FCSTD DOCUMENT  (FreeCAD 1.0R39109 (Git))
Label: DisplayAssembly
License: All rights reserved
LicenseURL: http://en.wikipedia.org/wiki/All_rights_reserved
objects: App::Link×5, App::FeaturePython×1, Assembly::JointGroup×1, Assembly::AssemblyObject×1
EXTERNAL_REF file=DICLEDBoard.FCStd obj=LED_Ring_1
EXTERNAL_REF file=DICDispalyBoard.FCStd obj=Scale
EXTERNAL_REF file=DICMainboard.FCStd obj=Board_e9e
EXTERNAL_REF file=ConnectorInterfaceBoard.FCStd obj=Board_5996
EXTERNAL_REF file=DICAddonBoard.FCStd obj=Board_25db

FEATURE [App::Link] LED_Ring_1  label="LED_Ring 1"
  LinkPlacement = pos=(45.9471,-39.3124,2.60361) rot=(0,0,1;0rad)
  LinkedObject = -> <external DICLEDBoard.FCStd>#LED_Ring_1
  Placement = pos=(45.9471,-39.3124,2.60361) rot=(0,0,1;0rad)
FEATURE [App::Link] Scale
  LinkPlacement = pos=(46.0527,-39.5665,0.857087) rot=(-0.468143,-0.288127,-0.835359;0.008707rad)
  LinkedObject = -> <external DICDispalyBoard.FCStd>#Scale
  Placement = pos=(46.0527,-39.5665,0.857087) rot=(-0.468143,-0.288127,-0.835359;0.008707rad)
FEATURE [App::Link] DIC
  LinkedObject = -> <external DICMainboard.FCStd>#Board_e9e
FEATURE [App::FeaturePython] GroundedJoint  # Assembly grounded joint (typed FeaturePython)
  ObjectToGround = -> DIC
FEATURE [Assembly::JointGroup] Joints
  Group = -> [GroundedJoint]
FEATURE [App::Link] ConnectorInterfaceBoard
  LinkPlacement = pos=(1.90735e-06,-68.64,-15.5) rot=(1,0,0;3.14159rad)
  LinkedObject = -> <external ConnectorInterfaceBoard.FCStd>#Board_5996
  Placement = pos=(1.90735e-06,-68.64,-15.5) rot=(1,0,0;3.14159rad)
FEATURE [App::Link] DIC_Addon
  LinkPlacement = pos=(-9.53674e-07,0,-7) rot=(0,0,1;0rad)
  LinkedObject = -> <external DICAddonBoard.FCStd>#Board_25db
  Placement = pos=(-9.53674e-07,0,-7) rot=(0,0,1;0rad)
FEATURE [Assembly::AssemblyObject] Assembly
  Group = -> [Joints,LED_Ring_1,Scale,DIC,GroundedJoint,ConnectorInterfaceBoard,DIC_Addon]
  Origin = -> Origin
  Type = Assembly

RESOLVED EXTERNAL PARTS (link-assembly join: the EXTERNAL_REF files above that resolve inside this repo's crawl, each included once):
---- part ConnectorInterfaceBoard.FCStd = doc fcstd_b694cefa8e00 ----
FCSTD DOCUMENT  (FreeCAD 1.0R39109 (Git))
Label: ConnectorInterfaceBoard
License: All rights reserved
LicenseURL: http://en.wikipedia.org/wiki/All_rights_reserved
objects: Part::Feature×9, App::Part×4, App::Link×2, PartDesign::CoordinateSystem×1, Sketcher::SketchObject×1
note: 12 computed .brp shape members not serialized (recipe doc carries the construction recipe); baked Part::Feature solids carry a one-line shape summary decoded from their .brp

FEATURE [PartDesign::CoordinateSystem] Local_CS_5996
  AttacherType = Attacher::AttachEngine3D
  MapMode = 2
FEATURE [Part::Feature] Pcb_5996
  shape: bbox 56.9 x 16.76 x 1.6 mm, 40 faces (baked)
FEATURE [Sketcher::SketchObject] PCB_Sketch_5996
  ArcFitTolerance = 1e-06
  FullyConstrained = false
  MakeInternals = false
  sketch-geometry (4):
    g0: LineSegment StartX=11.938 StartY=-11.938 StartZ=0 EndX=68.834 EndY=-11.938 EndZ=0
    g1: LineSegment StartX=68.834 StartY=-11.938 StartZ=0 EndX=68.834 EndY=-28.702 EndZ=0
    g2: LineSegment StartX=68.834 StartY=-28.702 StartZ=0 EndX=11.938 EndY=-28.702 EndZ=0
    g3: LineSegment StartX=11.938 StartY=-28.702 StartZ=0 EndX=11.938 EndY=-11.938 EndZ=0
  constraints (4):
    c: Coincident(g2,g3)
    c: Coincident(g0,g3)
    c: Coincident(g1,g2)
    c: Coincident(g0,g1)
FEATURE [Part::Feature] Shape  label="J4_PinHeader_2x08_P127mm_Vertical_934e7c050846"
  Placement = pos=(16.7132,-15.875,0) rot=(0,0,1;0rad)
  shape: bbox 3.4 x 10.16 x 6.3 mm, 340 faces (baked)
FEATURE [Part::Feature] Shape001  label="J1_RT3MP_764b897103e7"
  Placement = pos=(28.829,-20.3708,16.5) rot=(0,1,0;1.5708rad)
  shape: bbox 12 x 12 x 20.5 mm, 41 faces (baked)
FEATURE [App::Link] J1_RT3MP_764b897103e7_ln_  label="J3_RT3MP_9311650603bd"
  LinkPlacement = pos=(62.865,-20.3708,16.5) rot=(0.57735,0.57735,-0.57735;2.0944rad)
  LinkedObject = -> Shape001
  Placement = pos=(62.865,-20.3708,16.5) rot=(0.57735,0.57735,-0.57735;2.0944rad)
FEATURE [App::Link] J1_RT3MP_764b897103e7_ln_001  label="J2_RT3MP_923871eb31ec"
  LinkPlacement = pos=(45.8216,-20.3962,16.5) rot=(0,1,0;1.5708rad)
  LinkedObject = -> Shape001
  Placement = pos=(45.8216,-20.3962,16.5) rot=(0,1,0;1.5708rad)
FEATURE [App::Part] Top_5996
  Group = -> [Shape,Shape001,J1_RT3MP_764b897103e7_ln_,J1_RT3MP_764b897103e7_ln_001]
  Origin = -> Origin003
FEATURE [App::Part] Step_Models_5996
  Group = -> [Top_5996]
  Origin = -> Origin002
FEATURE [Part::Feature] pads_area001  label="topPads_5996"
  Placement = pos=(0,0,0.02) rot=(0,0,1;0rad)
  shape: bbox 52.14 x 13.81 x 2e-07 mm, 53 faces, 0 solids (baked)
FEATURE [Part::Feature] Shape003  label="topTracks_5996"
  Placement = pos=(0,0,0.01) rot=(0,0,1;0rad)
  shape: bbox 46.46 x 15.71 x 2e-07 mm, 15 faces, 0 solids (baked)
FEATURE [Part::Feature] zones_area001  label="topZones_5996"
  Placement = pos=(0,0,0.01) rot=(0,0,1;0rad)
  shape: bbox 56.8 x 16.66 x 2e-07 mm, 9 faces, 0 solids (baked)
FEATURE [Part::Feature] pads_area003  label="botPads_5996"
  Placement = pos=(0,0,-1.62) rot=(0,0,1;0rad)
  shape: bbox 52.14 x 13.81 x 2e-07 mm, 53 faces, 0 solids (baked)
FEATURE [Part::Feature] Shape005  label="botTracks_5996"
  Placement = pos=(0,0,-1.61) rot=(0,0,1;0rad)
  shape: bbox 53.24 x 14.74 x 2e-07 mm, 12 faces, 0 solids (baked)
FEATURE [Part::Feature] zones_area003  label="botZones_5996"
  Placement = pos=(0,0,-1.61) rot=(0,0,1;0rad)
  shape: bbox 56.8 x 16.66 x 2e-07 mm, 1 faces, 0 solids (baked)
FEATURE [App::Part] Board_Geoms_5996
  Group = -> [Pcb_5996,PCB_Sketch_5996,pads_area001,Shape003,zones_area001,pads_area003,Shape005,zones_area003]
  Origin = -> Origin
FEATURE [App::Part] Board_5996  label="ConnectorInterfaceBoard"
  Group = -> [Local_CS_5996,Board_Geoms_5996,Step_Models_5996]
  Origin = -> Origin001
---- part DICAddonBoard.FCStd = doc fcstd_c73b9f38876c ----
FCSTD DOCUMENT  (FreeCAD 1.0R39109 (Git))
Label: DICAddonBoard
License: All rights reserved
LicenseURL: http://en.wikipedia.org/wiki/All_rights_reserved
objects: App::Link×70, Part::Feature×18, App::Part×5, PartDesign::CoordinateSystem×1, Sketcher::SketchObject×1
note: 21 computed .brp shape members not serialized (recipe doc carries the construction recipe); baked Part::Feature solids carry a one-line shape summary decoded from their .brp

FEATURE [PartDesign::CoordinateSystem] Local_CS_25db
  AttacherType = Attacher::AttachEngine3D
  MapMode = 2
FEATURE [Part::Feature] Pcb_25db
  shape: bbox 67.95 x 50.29 x 1.6 mm, 68 faces (baked)
FEATURE [Sketcher::SketchObject] PCB_Sketch_25db
  ArcFitTolerance = 1e-06
  FullyConstrained = false
  MakeInternals = false
  sketch-geometry (10):
    g0: LineSegment StartX=11.938 StartY=-11.938 StartZ=0 EndX=11.938 EndY=-62.23 EndZ=0
    g1: LineSegment StartX=68.58 StartY=-62.103 StartZ=0 EndX=79.883 EndY=-62.103 EndZ=0
    g2: LineSegment StartX=11.938 StartY=-62.23 StartZ=0 EndX=23.3806 EndY=-62.23 EndZ=0
    g3: LineSegment StartX=23.3806 StartY=-62.23 StartZ=0 EndX=23.368 EndY=-55.9897 EndZ=0
    g4: LineSegment StartX=79.756 StartY=-11.938 StartZ=0 EndX=11.938 EndY=-11.938 EndZ=0
    g5: LineSegment StartX=68.5926 StartY=-55.8627 StartZ=0 EndX=68.58 EndY=-62.103 EndZ=0
    g6: LineSegment StartX=28.448 StartY=-50.673 StartZ=0 EndX=63.5588 EndY=-50.6595 EndZ=0
    g7: LineSegment StartX=79.883 StartY=-62.103 StartZ=0 EndX=79.756 EndY=-11.938 EndZ=0
    g8: ArcOfCircle CenterX=28.5729 CenterY=-55.8776 CenterZ=0 NormalX=0 NormalY=0 NormalZ=-1 AngleXU=-0.0215457 Radius=5.20607 StartAngle=0 EndAngle=1.56835
    g9: ArcOfCircle CenterX=63.5 CenterY=-55.753 CenterZ=0 NormalX=0 NormalY=0 NormalZ=-1 AngleXU=1.58235 Radius=5.09379 StartAngle=-4.7832e-11 EndAngle=1.58079
  constraints (10):
    c: Coincident(g0,g2)
    c: Coincident(g0,g4)
    c: Coincident(g3,g8)
    c: Coincident(g2,g3)
    c: Coincident(g6,g8)
    c: Coincident(g6,g9)
    c: Coincident(g1,g5)
    c: Coincident(g5,g9)
    c: Coincident(g4,g7)
    c: Coincident(g1,g7)
FEATURE [Part::Feature] Shape  label="Q6_SOT_23_ffd5320711a5"
  Placement = pos=(37.211,-18.262,0) rot=(0,0,1;0rad)
  shape: bbox 2.5 x 3 x 1.2 mm, 76 faces (baked)
FEATURE [Part::Feature] Shape001  label="D16_D_SOD_323_d7651d96f6c3"
  Placement = pos=(13.7425,-40.366,0) rot=(0,0,1;1.5708rad)
  shape: bbox 1.25 x 2.5 x 1.1 mm, 67 faces (baked)
FEATURE [Part::Feature] Shape002  label="J6_PinSocket_2x05_P127mm_Vertical_83ee9fbb584e"
  Placement = pos=(16.891,-54.483,0) rot=(0,0,1;0rad)
  shape: bbox 3.05 x 6.35 x 7 mm, 320 faces (baked)
FEATURE [Part::Feature] Shape003  label="R41_R_0603_1608Metric_127fa2614279"
  Placement = pos=(16.433,-42.799,0) rot=(0,0,1;0rad)
  shape: bbox 1.6 x 0.8 x 0.45 mm, 26 faces (baked)
FEATURE [App::Link] R41_R_0603_1608Metric_127fa2614279_ln_  label="R12_R_0603_1608Metric_a0e0216bc4ce"
  LinkPlacement = pos=(29.9212,-15.0876,0) rot=(0,0,1;3.14159rad)
  LinkedObject = -> Shape003
  Placement = pos=(29.9212,-15.0876,0) rot=(0,0,1;3.14159rad)
FEATURE [App::Link] R41_R_0603_1608Metric_127fa2614279_ln_001  label="R13_R_0603_1608Metric_473b31106c1b"
  LinkPlacement = pos=(32.639,-18.77,0) rot=(0,0,1;1.5708rad)
  LinkedObject = -> Shape003
  Placement = pos=(32.639,-18.77,0) rot=(0,0,1;1.5708rad)
FEATURE [Part::Feature] Shape004  label="D6_D_SMA_735d77270f2b"
  Placement = pos=(55.477,-16.896,0) rot=(0,0,1;1.5708rad)
  shape: bbox 2.7 x 5 x 2.22 mm, 41 faces (baked)
FEATURE [App::Link] R41_R_0603_1608Metric_127fa2614279_ln_002  label="R9_R_0603_1608Metric_79f8a3dd54a6"
  LinkPlacement = pos=(61.214,-13.9059,0) rot=(0,0,1;3.14159rad)
  LinkedObject = -> Shape003
  Placement = pos=(61.214,-13.9059,0) rot=(0,0,1;3.14159rad)
FEATURE [App::Link] R41_R_0603_1608Metric_127fa2614279_ln_003  label="R31_R_0603_1608Metric_c49473b8d088"
  LinkPlacement = pos=(50.473,-46.8085,0) rot=(0,0,1;1.5708rad)
  LinkedObject = -> Shape003
  Placement = pos=(50.473,-46.8085,0) rot=(0,0,1;1.5708rad)
FEATURE [App::Link] R41_R_0603_1608Metric_127fa2614279_ln_004  label="R14_R_0603_1608Metric_d7197a96d642"
  LinkPlacement = pos=(37.41,-15.722,0) rot=(0,0,1;0rad)
  LinkedObject = -> Shape003
  Placement = pos=(37.41,-15.722,0) rot=(0,0,1;0rad)
FEATURE [App::Link] R41_R_0603_1608Metric_127fa2614279_ln_005  label="R35_R_0603_1608Metric_1226fcb64f1c"
  LinkPlacement = pos=(47.933,-37.9245,0) rot=(0,0,1;0rad)
  LinkedObject = -> Shape003
  Placement = pos=(47.933,-37.9245,0) rot=(0,0,1;0rad)
FEATURE [App::Link] D6_D_SMA_735d77270f2b_ln_  label="D17_D_SMA_0876cbf78d6f"
  LinkPlacement = pos=(20.828,-34.925,0) rot=(0,0,1;1.5708rad)
  LinkedObject = -> Shape004
  Placement = pos=(20.828,-34.925,0) rot=(0,0,1;1.5708rad)
FEATURE [App::Link] D6_D_SMA_735d77270f2b_ln_001  label="D15_D_SMA_1207fe425828"
  LinkPlacement = pos=(53.255,-43.21,0) rot=(0,0,1;0rad)
  LinkedObject = -> Shape004
  Placement = pos=(53.255,-43.21,0) rot=(0,0,1;0rad)
FEATURE [App::Link] D16_D_SOD_323_d7651d96f6c3_ln_  label="D13_D_SOD_323_07ad6b2cef4e"
  LinkPlacement = pos=(47.826,-32.3365,0) rot=(0,0,1;3.14159rad)
  LinkedObject = -> Shape001
  Placement = pos=(47.826,-32.3365,0) rot=(0,0,1;3.14159rad)
FEATURE [App::Link] R41_R_0603_1608Metric_127fa2614279_ln_006  label="R32_R_0603_1608Metric_48fbb2cf6ecc"
  LinkPlacement = pos=(56.061,-46.705,0) rot=(0,0,1;1.5708rad)
  LinkedObject = -> Shape003
  Placement = pos=(56.061,-46.705,0) rot=(0,0,1;1.5708rad)
FEATURE [App::Link] R41_R_0603_1608Metric_127fa2614279_ln_007  label="R24_R_0603_1608Metric_9565dda51c7b"
  LinkPlacement = pos=(50.461,-36.098,0) rot=(0,0,1;1.5708rad)
  LinkedObject = -> Shape003
  Placement = pos=(50.461,-36.098,0) rot=(0,0,1;1.5708rad)
FEATURE [App::Link] R41_R_0603_1608Metric_127fa2614279_ln_008  label="R39_R_0603_1608Metric_0d8059b3905e"
  LinkPlacement = pos=(27.857,-32.131,0) rot=(0,0,1;3.14159rad)
  LinkedObject = -> Shape003
  Placement = pos=(27.857,-32.131,0) rot=(0,0,1;3.14159rad)
FEATURE [App::Link] R41_R_0603_1608Metric_127fa2614279_ln_009  label="R11_R_0603_1608Metric_e8feb780e285"
  LinkPlacement = pos=(37.363,-14.198,0) rot=(0,0,1;0rad)
  LinkedObject = -> Shape003
  Placement = pos=(37.363,-14.198,0) rot=(0,0,1;0rad)
FEATURE [App::Link] D6_D_SMA_735d77270f2b_ln_002  label="D9_D_SMA_59bcf57c5f9f"
  LinkPlacement = pos=(51.943,-16.865,0) rot=(0,0,1;1.5708rad)
  LinkedObject = -> Shape004
  Placement = pos=(51.943,-16.865,0) rot=(0,0,1;1.5708rad)
FEATURE [App::Link] D6_D_SMA_735d77270f2b_ln_003  label="D18_D_SMA_56b2f2076145"
  LinkPlacement = pos=(24.362,-34.925,0) rot=(0,0,1;1.5708rad)
  LinkedObject = -> Shape004
  Placement = pos=(24.362,-34.925,0) rot=(0,0,1;1.5708rad)
FEATURE [App::Link] R41_R_0603_1608Metric_127fa2614279_ln_010  label="R37_R_0603_1608Metric_b9a5ae661070"
  LinkPlacement = pos=(17.25,-32.004,0) rot=(0,0,1;0rad)
  LinkedObject = -> Shape003
  Placement = pos=(17.25,-32.004,0) rot=(0,0,1;0rad)
FEATURE [App::Link] R41_R_0603_1608Metric_127fa2614279_ln_011  label="R34_R_0603_1608Metric_5b0c20e38f9c"
  LinkPlacement = pos=(44.504,-34.1145,0) rot=(0,0,1;3.14159rad)
  LinkedObject = -> Shape003
  Placement = pos=(44.504,-34.1145,0) rot=(0,0,1;3.14159rad)
FEATURE [App::Link] R41_R_0603_1608Metric_127fa2614279_ln_012  label="R33_R_0603_1608Metric_6760e7cc6251"
  LinkPlacement = pos=(44.0995,-32.3365,0) rot=(0,0,1;3.14159rad)
  LinkedObject = -> Shape003
  Placement = pos=(44.0995,-32.3365,0) rot=(0,0,1;3.14159rad)
FEATURE [App::Link] D16_D_SOD_323_d7651d96f6c3_ln_001  label="D4_D_SOD_323_fbe22daa305a"
  LinkPlacement = pos=(30.861,-18.2655,0) rot=(0,0,1;1.5708rad)
  LinkedObject = -> Shape001
  Placement = pos=(30.861,-18.2655,0) rot=(0,0,1;1.5708rad)
FEATURE [Part::Feature] Shape005  label="TH6_R_1206_3216Metric_a4174fc2a386"
  Placement = pos=(22.584,-39.624,0) rot=(0,0,1;3.14159rad)
  shape: bbox 3.2 x 1.6 x 0.55 mm, 26 faces (baked)
FEATURE [App::Link] R41_R_0603_1608Metric_127fa2614279_ln_013  label="R40_R_0603_1608Metric_99d0bb74b373"
  LinkPlacement = pos=(13.7425,-36.703,0) rot=(0,0,1;1.5708rad)
  LinkedObject = -> Shape003
  Placement = pos=(13.7425,-36.703,0) rot=(0,0,1;1.5708rad)
FEATURE [App::Link] R41_R_0603_1608Metric_127fa2614279_ln_014  label="R8_R_0603_1608Metric_f9849ceb0926"
  LinkPlacement = pos=(61.087,-19.4939,0) rot=(0,0,1;3.14159rad)
  LinkedObject = -> Shape003
  Placement = pos=(61.087,-19.4939,0) rot=(0,0,1;3.14159rad)
FEATURE [App::Link] R41_R_0603_1608Metric_127fa2614279_ln_015  label="R36_R_0603_1608Metric_b33a5e9c3cf1"
  LinkPlacement = pos=(17.377,-37.592,0) rot=(0,0,1;3.14159rad)
  LinkedObject = -> Shape003
  Placement = pos=(17.377,-37.592,0) rot=(0,0,1;3.14159rad)
FEATURE [App::Link] Q6_SOT_23_ffd5320711a5_ln_  label="Q18_SOT_23_5dae6c215293"
  LinkPlacement = pos=(16.6635,-40.259,0) rot=(0,0,1;3.14159rad)
  LinkedObject = -> Shape
  Placement = pos=(16.6635,-40.259,0) rot=(0,0,1;3.14159rad)
FEATURE [App::Link] J6_PinSocket_2x05_P127mm_Vertical_83ee9fbb584e_ln_  label="J2_PinSocket_2x05_P127mm_Vertical_fade8c78a2a7"
  LinkPlacement = pos=(76.2,-14.859,0) rot=(0,0,1;0rad)
  LinkedObject = -> Shape002
  Placement = pos=(76.2,-14.859,0) rot=(0,0,1;0rad)
FEATURE [App::Link] J6_PinSocket_2x05_P127mm_Vertical_83ee9fbb584e_ln_001  label="J5_PinSocket_2x05_P127mm_Vertical_c59673f5576a"
  LinkPlacement = pos=(16.129,-20.701,0) rot=(0,0,1;3.14159rad)
  LinkedObject = -> Shape002
  Placement = pos=(16.129,-20.701,0) rot=(0,0,1;3.14159rad)
FEATURE [App::Link] TH6_R_1206_3216Metric_a4174fc2a386_ln_  label="TH2_R_1206_3216Metric_52bc38417804"
  LinkPlacement = pos=(41.529,-18.262,0) rot=(0,0,1;1.5708rad)
  LinkedObject = -> Shape005
  Placement = pos=(41.529,-18.262,0) rot=(0,0,1;1.5708rad)
FEATURE [App::Link] D6_D_SMA_735d77270f2b_ln_004  label="D14_D_SMA_40db2f55f09c"
  LinkPlacement = pos=(53.255,-39.584,0) rot=(0,0,1;0rad)
  LinkedObject = -> Shape004
  Placement = pos=(53.255,-39.584,0) rot=(0,0,1;0rad)
FEATURE [App::Link] R41_R_0603_1608Metric_127fa2614279_ln_016  label="R42_R_0603_1608Metric_3962cb7ffa21"
  LinkPlacement = pos=(19.3305,-40.386,0) rot=(0,0,1;1.5708rad)
  LinkedObject = -> Shape003
  Placement = pos=(19.3305,-40.386,0) rot=(0,0,1;1.5708rad)
FEATURE [App::Link] J6_PinSocket_2x05_P127mm_Vertical_83ee9fbb584e_ln_002  label="J4_PinSocket_2x05_P127mm_Vertical_839abc38b667"
  LinkPlacement = pos=(75.819,-54.473,0) rot=(0,0,1;0rad)
  LinkedObject = -> Shape002
  Placement = pos=(75.819,-54.473,0) rot=(0,0,1;0rad)
FEATURE [App::Link] R41_R_0603_1608Metric_127fa2614279_ln_017  label="R10_R_0603_1608Metric_f7e09fcf0586"
  LinkPlacement = pos=(48.387,-13.563,0) rot=(0,0,1;3.14159rad)
  LinkedObject = -> Shape003
  Placement = pos=(48.387,-13.563,0) rot=(0,0,1;3.14159rad)
FEATURE [App::Link] R41_R_0603_1608Metric_127fa2614279_ln_018  label="R38_R_0603_1608Metric_5053fa264887"
  LinkPlacement = pos=(27.984,-37.719,0) rot=(0,0,1;3.14159rad)
  LinkedObject = -> Shape003
  Placement = pos=(27.984,-37.719,0) rot=(0,0,1;3.14159rad)
FEATURE [App::Link] R41_R_0603_1608Metric_127fa2614279_ln_019  label="R30_R_0603_1608Metric_0ef8a02bf31b"
  LinkPlacement = pos=(56.061,-36.0085,0) rot=(0,0,-1;1.5708rad)
  LinkedObject = -> Shape003
  Placement = pos=(56.061,-36.0085,0) rot=(0,0,-1;1.5708rad)
FEATURE [App::Link] Q6_SOT_23_ffd5320711a5_ln_001  label="Q15_SOT_23_f88ca606a138"
  LinkPlacement = pos=(47.933,-35.2575,0) rot=(0,0,1;1.5708rad)
  LinkedObject = -> Shape
  Placement = pos=(47.933,-35.2575,0) rot=(0,0,1;1.5708rad)
FEATURE [App::Link] TH6_R_1206_3216Metric_a4174fc2a386_ln_001  label="TH4_R_1206_3216Metric_6cedd577e318"
  LinkPlacement = pos=(48.568,-41.178,0) rot=(0,0,1;1.5708rad)
  LinkedObject = -> Shape005
  Placement = pos=(48.568,-41.178,0) rot=(0,0,1;1.5708rad)
FEATURE [App::Part] Top_25db
  Group = -> [Shape,Shape001,Shape002,Shape003,R41_R_0603_1608Metric_127fa2614279_ln_,R41_R_0603_1608Metric_127fa2614279_ln_001,Shape004,R41_R_0603_1608Metric_127fa2614279_ln_002,R41_R_0603_1608Metric_127fa2614279_ln_003,R41_R_0603_1608Metric_127fa2614279_ln_004,R41_R_0603_1608Metric_127fa2614279_ln_005,D6_D_SMA_735d77270f2b_ln_,D6_D_SMA_735d77270f2b_ln_001,D16_D_SOD_323_d7651d96f6c3_ln_,+26 more]
  Origin = -> Origin003
FEATURE [App::Link] R41_R_0603_1608Metric_127fa2614279_ln_020  label="R16_R_0603_1608Metric_7932c1e08af1"
  LinkPlacement = pos=(41.275,-42.313,-1.6) rot=(0.707107,0.707107,0;3.14159rad)
  LinkedObject = -> Shape003
  Placement = pos=(41.275,-42.313,-1.6) rot=(0.707107,0.707107,0;3.14159rad)
FEATURE [App::Link] R41_R_0603_1608Metric_127fa2614279_ln_021  label="R25_R_0603_1608Metric_af43064dc6b6"
  LinkPlacement = pos=(74.996,-34.8215,-1.6) rot=(0.707107,-0.707107,0;3.14159rad)
  LinkedObject = -> Shape003
  Placement = pos=(74.996,-34.8215,-1.6) rot=(0.707107,-0.707107,0;3.14159rad)
FEATURE [App::Link] R41_R_0603_1608Metric_127fa2614279_ln_022  label="R3_R_0603_1608Metric_90eb9fac611c"
  LinkPlacement = pos=(27.8525,-37.777,-1.6) rot=(0.707107,0.707107,0;3.14159rad)
  LinkedObject = -> Shape003
  Placement = pos=(27.8525,-37.777,-1.6) rot=(0.707107,0.707107,0;3.14159rad)
FEATURE [App::Link] R41_R_0603_1608Metric_127fa2614279_ln_023  label="R2_R_0603_1608Metric_a95339afed33"
  LinkPlacement = pos=(22.3534,-27.095,-1.6) rot=(0.707107,0.707107,0;3.14159rad)
  LinkedObject = -> Shape003
  Placement = pos=(22.3534,-27.095,-1.6) rot=(0.707107,0.707107,0;3.14159rad)
FEATURE [App::Link] R41_R_0603_1608Metric_127fa2614279_ln_024  label="R29_R_0603_1608Metric_a323e5d2541c"
  LinkPlacement = pos=(69.088,-31.2255,-1.6) rot=(0.707107,-0.707107,0;3.14159rad)
  LinkedObject = -> Shape003
  Placement = pos=(69.088,-31.2255,-1.6) rot=(0.707107,-0.707107,0;3.14159rad)
FEATURE [App::Link] R41_R_0603_1608Metric_127fa2614279_ln_025  label="R1_R_0603_1608Metric_b07fb1c3085f"
  LinkPlacement = pos=(27.9414,-27.222,-1.6) rot=(0.707107,0.707107,0;3.14159rad)
  LinkedObject = -> Shape003
  Placement = pos=(27.9414,-27.222,-1.6) rot=(0.707107,0.707107,0;3.14159rad)
FEATURE [App::Link] R41_R_0603_1608Metric_127fa2614279_ln_026  label="R18_R_0603_1608Metric_5d82281689e8"
  LinkPlacement = pos=(26.7885,-42.672,-1.6) rot=(0,1,0;3.14159rad)
  LinkedObject = -> Shape003
  Placement = pos=(26.7885,-42.672,-1.6) rot=(0,1,0;3.14159rad)
FEATURE [App::Link] R41_R_0603_1608Metric_127fa2614279_ln_027  label="R27_R_0603_1608Metric_214af474eae8"
  LinkPlacement = pos=(75.9085,-41.275,-1.6) rot=(1,0,0;3.14159rad)
  LinkedObject = -> Shape003
  Placement = pos=(75.9085,-41.275,-1.6) rot=(1,0,0;3.14159rad)
FEATURE [App::Link] D6_D_SMA_735d77270f2b_ln_005  label="D11_D_SMA_1ba17688d2f4"
  LinkPlacement = pos=(38.449,-38.735,-1.6) rot=(1,0,0;3.14159rad)
  LinkedObject = -> Shape004
  Placement = pos=(38.449,-38.735,-1.6) rot=(1,0,0;3.14159rad)
FEATURE [App::Link] R41_R_0603_1608Metric_127fa2614279_ln_028  label="R17_R_0603_1608Metric_89ce4ec7833c"
  LinkPlacement = pos=(26.8355,-48.26,-1.6) rot=(1,0,0;3.14159rad)
  LinkedObject = -> Shape003
  Placement = pos=(26.8355,-48.26,-1.6) rot=(1,0,0;3.14159rad)
FEATURE [App::Link] R41_R_0603_1608Metric_127fa2614279_ln_029  label="R6_R_0603_1608Metric_1afd86b5277d"
  LinkPlacement = pos=(35.7265,-28.421,-1.6) rot=(0.707107,0.707107,0;3.14159rad)
  LinkedObject = -> Shape003
  Placement = pos=(35.7265,-28.421,-1.6) rot=(0.707107,0.707107,0;3.14159rad)
FEATURE [App::Link] D16_D_SOD_323_d7651d96f6c3_ln_002  label="D10_D_SOD_323_00e277693b72"
  LinkPlacement = pos=(33.167,-46.0745,-1.6) rot=(0,1,0;3.14159rad)
  LinkedObject = -> Shape001
  Placement = pos=(33.167,-46.0745,-1.6) rot=(0,1,0;3.14159rad)
FEATURE [Part::Feature] Shape006  label="J3_PinHeader_2x08_P127mm_Vertical_13ff719d442c"
  Placement = pos=(50.551,-23.866,-1.6) rot=(0.707107,0.707107,0;3.14159rad)
  shape: bbox 10.16 x 3.4 x 6.3 mm, 340 faces (baked)
FEATURE [App::Link] D6_D_SMA_735d77270f2b_ln_006  label="D3_D_SMA_cd35c1e422c8"
  LinkPlacement = pos=(25.0905,-34.268,-1.6) rot=(0,1,0;3.14159rad)
  LinkedObject = -> Shape004
  Placement = pos=(25.0905,-34.268,-1.6) rot=(0,1,0;3.14159rad)
FEATURE [App::Link] R41_R_0603_1608Metric_127fa2614279_ln_030  label="R7_R_0603_1608Metric_afc0888e760f"
  LinkPlacement = pos=(30.6465,-28.172,-1.6) rot=(0.707107,-0.707107,0;3.14159rad)
  LinkedObject = -> Shape003
  Placement = pos=(30.6465,-28.172,-1.6) rot=(0.707107,-0.707107,0;3.14159rad)
FEATURE [App::Link] R41_R_0603_1608Metric_127fa2614279_ln_031  label="R28_R_0603_1608Metric_a4707fec901c"
  LinkPlacement = pos=(61.595,-31.0515,-1.6) rot=(0.707107,0.707107,0;3.14159rad)
  LinkedObject = -> Shape003
  Placement = pos=(61.595,-31.0515,-1.6) rot=(0.707107,0.707107,0;3.14159rad)
FEATURE [App::Link] D16_D_SOD_323_d7651d96f6c3_ln_003  label="D5_D_SOD_323_8140ef0d37c0"
  LinkPlacement = pos=(63.373,-31.095,-1.6) rot=(0.707107,0.707107,0;3.14159rad)
  LinkedObject = -> Shape001
  Placement = pos=(63.373,-31.095,-1.6) rot=(0.707107,0.707107,0;3.14159rad)
FEATURE [App::Link] D16_D_SOD_323_d7651d96f6c3_ln_004  label="D1_D_SOD_323_d5d77308ac17"
  LinkPlacement = pos=(33.1665,-31.347,-1.6) rot=(1,0,0;3.14159rad)
  LinkedObject = -> Shape001
  Placement = pos=(33.1665,-31.347,-1.6) rot=(1,0,0;3.14159rad)
FEATURE [App::Link] Q6_SOT_23_ffd5320711a5_ln_002  label="Q10_SOT_23_8cad5c28a702"
  LinkPlacement = pos=(33.147,-43.0265,-1.6) rot=(0.707107,-0.707107,0;3.14159rad)
  LinkedObject = -> Shape
  Placement = pos=(33.147,-43.0265,-1.6) rot=(0.707107,-0.707107,0;3.14159rad)
FEATURE [App::Link] R41_R_0603_1608Metric_127fa2614279_ln_032  label="R23_R_0603_1608Metric_7848ec0b3468"
  LinkPlacement = pos=(65.151,-41.529,-1.6) rot=(1,0,0;3.14159rad)
  LinkedObject = -> Shape003
  Placement = pos=(65.151,-41.529,-1.6) rot=(1,0,0;3.14159rad)
FEATURE [App::Link] TH6_R_1206_3216Metric_a4174fc2a386_ln_002  label="TH5_R_1206_3216Metric_65273da20f15"
  LinkPlacement = pos=(70.612,-34.036,-1.6) rot=(0,1,0;3.14159rad)
  LinkedObject = -> Shape005
  Placement = pos=(70.612,-34.036,-1.6) rot=(0,1,0;3.14159rad)
FEATURE [App::Link] R41_R_0603_1608Metric_127fa2614279_ln_033  label="R19_R_0603_1608Metric_b451ed5a0d5d"
  LinkPlacement = pos=(29.845,-41.021,-1.6) rot=(0.707107,-0.707107,0;3.14159rad)
  LinkedObject = -> Shape003
  Placement = pos=(29.845,-41.021,-1.6) rot=(0.707107,-0.707107,0;3.14159rad)
FEATURE [App::Link] R41_R_0603_1608Metric_127fa2614279_ln_034  label="R21_R_0603_1608Metric_086685fbb64e"
  LinkPlacement = pos=(64.262,-35.0285,-1.6) rot=(0.707107,0.707107,0;3.14159rad)
  LinkedObject = -> Shape003
  Placement = pos=(64.262,-35.0285,-1.6) rot=(0.707107,0.707107,0;3.14159rad)
FEATURE [App::Link] R41_R_0603_1608Metric_127fa2614279_ln_035  label="R20_R_0603_1608Metric_74876393d18b"
  LinkPlacement = pos=(37.211,-46.0745,-1.6) rot=(1,0,0;3.14159rad)
  LinkedObject = -> Shape003
  Placement = pos=(37.211,-46.0745,-1.6) rot=(1,0,0;3.14159rad)
FEATURE [App::Link] R41_R_0603_1608Metric_127fa2614279_ln_036  label="R15_R_0603_1608Metric_62f7b17bc8fc"
  LinkPlacement = pos=(35.687,-42.313,-1.6) rot=(0.707107,-0.707107,0;3.14159rad)
  LinkedObject = -> Shape003
  Placement = pos=(35.687,-42.313,-1.6) rot=(0.707107,-0.707107,0;3.14159rad)
FEATURE [App::Link] D6_D_SMA_735d77270f2b_ln_007  label="D2_D_SMA_e8f0f4ea1691"
  LinkPlacement = pos=(25.0905,-30.734,-1.6) rot=(0,1,0;3.14159rad)
  LinkedObject = -> Shape004
  Placement = pos=(25.0905,-30.734,-1.6) rot=(0,1,0;3.14159rad)
FEATURE [App::Link] TH6_R_1206_3216Metric_a4174fc2a386_ln_003  label="TH1_R_1206_3216Metric_ce9414de59a2"
  LinkPlacement = pos=(29.8845,-32.617,-1.6) rot=(0.707107,0.707107,0;3.14159rad)
  LinkedObject = -> Shape005
  Placement = pos=(29.8845,-32.617,-1.6) rot=(0.707107,0.707107,0;3.14159rad)
FEATURE [App::Link] D6_D_SMA_735d77270f2b_ln_008  label="D12_D_SMA_21d0ff51f2b2"
  LinkPlacement = pos=(38.449,-35.201,-1.6) rot=(1,0,0;3.14159rad)
  LinkedObject = -> Shape004
  Placement = pos=(38.449,-35.201,-1.6) rot=(1,0,0;3.14159rad)
FEATURE [App::Link] TH6_R_1206_3216Metric_a4174fc2a386_ln_004  label="TH3_R_1206_3216Metric_be97d367e00d"
  LinkPlacement = pos=(33.782,-36.852,-1.6) rot=(0.707107,-0.707107,0;3.14159rad)
  LinkedObject = -> Shape005
  Placement = pos=(33.782,-36.852,-1.6) rot=(0.707107,-0.707107,0;3.14159rad)
FEATURE [App::Link] D6_D_SMA_735d77270f2b_ln_009  label="D8_D_SMA_7218f854b2e2"
  LinkPlacement = pos=(72.39,-38.703,-1.6) rot=(0.707107,-0.707107,0;3.14159rad)
  LinkedObject = -> Shape004
  Placement = pos=(72.39,-38.703,-1.6) rot=(0.707107,-0.707107,0;3.14159rad)
FEATURE [App::Link] Q6_SOT_23_ffd5320711a5_ln_003  label="Q3_SOT_23_dc7f19c19d1b"
  LinkPlacement = pos=(33.1865,-28.299,-1.6) rot=(0.707107,-0.707107,0;3.14159rad)
  LinkedObject = -> Shape
  Placement = pos=(33.1865,-28.299,-1.6) rot=(0.707107,-0.707107,0;3.14159rad)
FEATURE [App::Link] R41_R_0603_1608Metric_127fa2614279_ln_037  label="R4_R_0603_1608Metric_2e89caf32d98"
  LinkPlacement = pos=(22.2645,-37.8005,-1.6) rot=(0.707107,-0.707107,0;3.14159rad)
  LinkedObject = -> Shape003
  Placement = pos=(22.2645,-37.8005,-1.6) rot=(0.707107,-0.707107,0;3.14159rad)
FEATURE [App::Link] R41_R_0603_1608Metric_127fa2614279_ln_038  label="R22_R_0603_1608Metric_94414fea2e43"
  LinkPlacement = pos=(33.1235,-40.3595,-1.6) rot=(1,0,0;3.14159rad)
  LinkedObject = -> Shape003
  Placement = pos=(33.1235,-40.3595,-1.6) rot=(1,0,0;3.14159rad)
FEATURE [App::Link] D6_D_SMA_735d77270f2b_ln_010  label="D7_D_SMA_2e44e889cb4e"
  LinkPlacement = pos=(68.834,-38.703,-1.6) rot=(0.707107,-0.707107,0;3.14159rad)
  LinkedObject = -> Shape004
  Placement = pos=(68.834,-38.703,-1.6) rot=(0.707107,-0.707107,0;3.14159rad)
FEATURE [App::Link] R41_R_0603_1608Metric_127fa2614279_ln_039  label="R26_R_0603_1608Metric_d41138b5fa4f"
  LinkPlacement = pos=(64.389,-28.281,-1.6) rot=(1,0,0;3.14159rad)
  LinkedObject = -> Shape003
  Placement = pos=(64.389,-28.281,-1.6) rot=(1,0,0;3.14159rad)
FEATURE [App::Link] Q6_SOT_23_ffd5320711a5_ln_004  label="Q12_SOT_23_6e3906f2bc9c"
  LinkPlacement = pos=(66.421,-31.202,-1.6) rot=(0,1,0;3.14159rad)
  LinkedObject = -> Shape
  Placement = pos=(66.421,-31.202,-1.6) rot=(0,1,0;3.14159rad)
FEATURE [App::Link] R41_R_0603_1608Metric_127fa2614279_ln_040  label="R5_R_0603_1608Metric_a69d22cc4bcb"
  LinkPlacement = pos=(37.719,-30.353,-1.6) rot=(0.707107,0.707107,0;3.14159rad)
  LinkedObject = -> Shape003
  Placement = pos=(37.719,-30.353,-1.6) rot=(0.707107,0.707107,0;3.14159rad)
FEATURE [App::Part] Bot_25db
  Group = -> [R41_R_0603_1608Metric_127fa2614279_ln_020,R41_R_0603_1608Metric_127fa2614279_ln_021,R41_R_0603_1608Metric_127fa2614279_ln_022,R41_R_0603_1608Metric_127fa2614279_ln_023,R41_R_0603_1608Metric_127fa2614279_ln_024,R41_R_0603_1608Metric_127fa2614279_ln_025,R41_R_0603_1608Metric_127fa2614279_ln_026,R41_R_0603_1608Metric_127fa2614279_ln_027,D6_D_SMA_735d77270f2b_ln_005,+28 more]
  Origin = -> Origin004
FEATURE [App::Part] Step_Models_25db
  Group = -> [Top_25db,Bot_25db]
  Origin = -> Origin002
FEATURE [Part::Feature] pads_area001  label="topPads_25db"
  Placement = pos=(0,0,0.02) rot=(0,0,1;0rad)
  shape: bbox 65.44 x 47.07 x 2e-07 mm, 247 faces, 0 solids (baked)
FEATURE [Part::Feature] Shape008  label="topTracks_25db"
  Placement = pos=(0,0,0.01) rot=(0,0,1;0rad)
  shape: bbox 65.02 x 45.59 x 2e-07 mm, 81 faces, 0 solids (baked)
FEATURE [Part::Feature] pads_area003  label="botPads_25db"
  Placement = pos=(0,0,-1.62) rot=(0,0,1;0rad)
  shape: bbox 65.44 x 47.03 x 2e-07 mm, 248 faces, 0 solids (baked)
FEATURE [Part::Feature] Shape010  label="botTracks_25db"
  Placement = pos=(0,0,-1.61) rot=(0,0,1;0rad)
  shape: bbox 65.32 x 46.99 x 2e-07 mm, 80 faces, 0 solids (baked)
FEATURE [Part::Feature] botSilks_c76e
  Placement = pos=(0,0,-1.67) rot=(0,0,1;0rad)
  shape: bbox 83.53 x 49.14 x 2e-07 mm, 230 faces, 0 solids (baked)
FEATURE [Part::Feature] topSilks_caba
  Placement = pos=(0,0,0.07) rot=(0,0,1;0rad)
  shape: bbox 64.67 x 49.71 x 2e-07 mm, 286 faces, 0 solids (baked)
FEATURE [Part::Feature] Part__Feature  label="1"
  Placement = pos=(16.4,-27.2,-1.6) rot=(0,1,0;3.14159rad)
  shape: bbox 6 x 6 x 5.6 mm, 7 faces (baked)
FEATURE [Part::Feature] Part__Feature001  label="1001"
  Placement = pos=(67.9,-16.9,-1.6) rot=(0,1,0;3.14159rad)
  shape: bbox 6 x 6 x 5.6 mm, 7 faces (baked)
FEATURE [Part::Feature] Part__Feature002  label="1002"
  Placement = pos=(16.4,-48,-1.6) rot=(0,1,0;3.14159rad)
  shape: bbox 6 x 6 x 5.6 mm, 7 faces (baked)
FEATURE [Part::Feature] Part__Feature003  label="1003"
  Placement = pos=(74.4,-47.8,-1.6) rot=(0,1,0;3.14159rad)
  shape: bbox 6 x 6 x 5.6 mm, 7 faces (baked)
FEATURE [App::Part] Board_Geoms_25db
  Group = -> [Pcb_25db,PCB_Sketch_25db,pads_area001,Shape008,pads_area003,Shape010,botSilks_c76e,topSilks_caba,Part__Feature,Part__Feature001,Part__Feature002,Part__Feature003]
  Origin = -> Origin
FEATURE [App::Part] Board_25db  label="DIC_Addon"
  Group = -> [Local_CS_25db,Board_Geoms_25db,Step_Models_25db]
  Origin = -> Origin001
---- part DICDispalyBoard.FCStd = doc fcstd_930c7f865829 ----
FCSTD DOCUMENT  (FreeCAD 1.0R39109 (Git))
Label: DICDispalyBoard
License: All rights reserved
LicenseURL: http://en.wikipedia.org/wiki/All_rights_reserved
objects: Part::Feature×1, Part::Scale×1
note: 2 computed .brp shape members not serialized (recipe doc carries the construction recipe); baked Part::Feature solids carry a one-line shape summary decoded from their .brp

FEATURE [Part::Feature] Part__Feature  label="78901133-5F87-439E-955A-E59BF70E4BD8"
  shape: bbox 55 x 43.5 x 6.701 mm, 1221 faces, 4 solids (baked)
FEATURE [Part::Scale] Scale
  Base = -> Part__Feature
  Uniform = false
  UniformScale = 1
  XScale = 1
  YScale = 1.12
  ZScale = 1
---- part DICMainboard.FCStd = doc fcstd_b85fe997ea7c ----
FCSTD DOCUMENT  (FreeCAD 1.0R39109 (Git))
Label: DICMainboard
License: All rights reserved
LicenseURL: http://en.wikipedia.org/wiki/All_rights_reserved
objects: App::Link×97, Part::Feature×24, App::Part×10, PartDesign::CoordinateSystem×1, Sketcher::SketchObject×1
note: 27 computed .brp shape members not serialized (recipe doc carries the construction recipe); baked Part::Feature solids carry a one-line shape summary decoded from their .brp

FEATURE [PartDesign::CoordinateSystem] Local_CS_e9e
  AttacherType = Attacher::AttachEngine3D
  MapMode = 2
FEATURE [Part::Feature] Pcb_e9e
  shape: bbox 68.07 x 55.25 x 1.6 mm, 110 faces (baked)
FEATURE [Sketcher::SketchObject] PCB_Sketch_e9e
  ArcFitTolerance = 1e-06
  FullyConstrained = true
  MakeInternals = false
FEATURE [Part::Feature] Shape  label="C19_C_0805_2012Metric_915db11c73f1"
  Placement = pos=(24.257,-16.448,-1.6) rot=(0.707107,0.707107,0;3.14159rad)
  shape: bbox 1.25 x 2 x 1.25 mm, 28 faces (baked)
FEATURE [Part::Feature] Shape001  label="C18_C_0603_1608Metric_10e447ca614a"
  Placement = pos=(39.878,-20.193,-1.6) rot=(1,0,0;3.14159rad)
  shape: bbox 1.6 x 0.8 x 0.8 mm, 28 faces (baked)
FEATURE [Part::Feature] Shape002  label="R42_R_0603_1608Metric_e00ced120b5b"
  Placement = pos=(70.993,-25.146,-1.6) rot=(1,0,0;3.14159rad)
  shape: bbox 1.6 x 0.8 x 0.45 mm, 26 faces (baked)
FEATURE [App::Link] R42_R_0603_1608Metric_e00ced120b5b_ln_  label="R3_R_0603_1608Metric_9b0ed8f2439a"
  LinkPlacement = pos=(35.687,-42.037,-1.6) rot=(1,0,0;3.14159rad)
  LinkedObject = -> Shape002
  Placement = pos=(35.687,-42.037,-1.6) rot=(1,0,0;3.14159rad)
FEATURE [App::Link] R42_R_0603_1608Metric_e00ced120b5b_ln_001  label="R2_R_0603_1608Metric_8df39385d074"
  LinkPlacement = pos=(27.265,-19.939,-1.6) rot=(0,1,0;3.14159rad)
  LinkedObject = -> Shape002
  Placement = pos=(27.265,-19.939,-1.6) rot=(0,1,0;3.14159rad)
FEATURE [Part::Feature] Shape003  label="C21_CP_Radial_D80mm_P350mm_b4bb79b80bd8"
  Placement = pos=(28.067,-57.531,-1.6) rot=(0.707107,0.707107,0;3.14159rad)
  shape: bbox 10.23 x 9.886 x 10 mm, 54 faces (baked)
FEATURE [App::Link] C19_C_0805_2012Metric_915db11c73f1_ln_  label="C12_C_0805_2012Metric_6993a4fefcef"
  LinkPlacement = pos=(29.972,-40.386,-1.6) rot=(0,1,0;3.14159rad)
  LinkedObject = -> Shape
  Placement = pos=(29.972,-40.386,-1.6) rot=(0,1,0;3.14159rad)
FEATURE [Part::Feature] Shape004  label="JTAG1_PinHeader_2x07_P127mm_Vertical_7ea92a9874db"
  Placement = pos=(76.835,-29.718,-1.6) rot=(0,1,0;3.14159rad)
  shape: bbox 3.4 x 8.89 x 6.3 mm, 298 faces (baked)
FEATURE [App::Link] R42_R_0603_1608Metric_e00ced120b5b_ln_002  label="R29_R_0603_1608Metric_b834401a76b2"
  LinkPlacement = pos=(60.579,-46.228,-1.6) rot=(0,1,0;3.14159rad)
  LinkedObject = -> Shape002
  Placement = pos=(60.579,-46.228,-1.6) rot=(0,1,0;3.14159rad)
FEATURE [App::Link] C18_C_0603_1608Metric_10e447ca614a_ln_  label="C29_C_0603_1608Metric_30aa2c5fb68f"
  LinkPlacement = pos=(50.546,-26.035,-1.6) rot=(1,0,0;3.14159rad)
  LinkedObject = -> Shape001
  Placement = pos=(50.546,-26.035,-1.6) rot=(1,0,0;3.14159rad)
FEATURE [App::Link] R42_R_0603_1608Metric_e00ced120b5b_ln_003  label="R36_R_0603_1608Metric_5693be527eb2"
  LinkPlacement = pos=(53.848,-26.035,-1.6) rot=(0,1,0;3.14159rad)
  LinkedObject = -> Shape002
  Placement = pos=(53.848,-26.035,-1.6) rot=(0,1,0;3.14159rad)
FEATURE [App::Link] R42_R_0603_1608Metric_e00ced120b5b_ln_004  label="R39_R_0603_1608Metric_50952633201f"
  LinkPlacement = pos=(69.215,-29.845,-1.6) rot=(0.707107,0.707107,0;3.14159rad)
  LinkedObject = -> Shape002
  Placement = pos=(69.215,-29.845,-1.6) rot=(0.707107,0.707107,0;3.14159rad)
FEATURE [Part::Feature] Shape005  label="U2_SOT_23_5143090a7d01"
  Placement = pos=(31.877,-43.688,-1.6) rot=(0.707107,-0.707107,0;3.14159rad)
  shape: bbox 3 x 2.5 x 1.2 mm, 76 faces (baked)
FEATURE [App::Link] U2_SOT_23_5143090a7d01_ln_  label="Q2_SOT_23_a46526c7cbaa"
  LinkPlacement = pos=(65.786,-38.735,-1.6) rot=(0.707107,0.707107,0;3.14159rad)
  LinkedObject = -> Shape005
  Placement = pos=(65.786,-38.735,-1.6) rot=(0.707107,0.707107,0;3.14159rad)
FEATURE [App::Link] R42_R_0603_1608Metric_e00ced120b5b_ln_005  label="R31_R_0603_1608Metric_b000aee3d83a"
  LinkPlacement = pos=(59.309,-28.702,-1.6) rot=(0,1,0;3.14159rad)
  LinkedObject = -> Shape002
  Placement = pos=(59.309,-28.702,-1.6) rot=(0,1,0;3.14159rad)
FEATURE [App::Link] C18_C_0603_1608Metric_10e447ca614a_ln_001  label="C5_C_0603_1608Metric_679d8c6e1927"
  LinkPlacement = pos=(34.417,-44.45,-1.6) rot=(0.707107,0.707107,0;3.14159rad)
  LinkedObject = -> Shape001
  Placement = pos=(34.417,-44.45,-1.6) rot=(0.707107,0.707107,0;3.14159rad)
FEATURE [App::Link] C18_C_0603_1608Metric_10e447ca614a_ln_002  label="C6_C_0603_1608Metric_e41e872100cf"
  LinkPlacement = pos=(39.116,-24.322,-1.6) rot=(0,1,0;3.14159rad)
  LinkedObject = -> Shape001
  Placement = pos=(39.116,-24.322,-1.6) rot=(0,1,0;3.14159rad)
FEATURE [Part::Feature] Shape006  label="12VGood1_LED_0805_2012Metric_2ad75f4ca093"
  Placement = pos=(69.469,-36.195,-1.6) rot=(0,1,0;3.14159rad)
  shape: bbox 2 x 1.25 x 1.1 mm, 50 faces (baked)
FEATURE [App::Link] C19_C_0805_2012Metric_915db11c73f1_ln_001  label="C14_C_0805_2012Metric_060f63ed2ef4"
  LinkPlacement = pos=(42.418,-49.911,-1.6) rot=(1,0,0;3.14159rad)
  LinkedObject = -> Shape
  Placement = pos=(42.418,-49.911,-1.6) rot=(1,0,0;3.14159rad)
FEATURE [App::Link] R42_R_0603_1608Metric_e00ced120b5b_ln_006  label="R30_R_0603_1608Metric_8c3fd63a3134"
  LinkPlacement = pos=(50.8,-42.926,-1.6) rot=(0,1,0;3.14159rad)
  LinkedObject = -> Shape002
  Placement = pos=(50.8,-42.926,-1.6) rot=(0,1,0;3.14159rad)
FEATURE [App::Link] C18_C_0603_1608Metric_10e447ca614a_ln_003  label="C17_C_0603_1608Metric_5bd1929c3623"
  LinkPlacement = pos=(39.878,-21.971,-1.6) rot=(1,0,0;3.14159rad)
  LinkedObject = -> Shape001
  Placement = pos=(39.878,-21.971,-1.6) rot=(1,0,0;3.14159rad)
FEATURE [App::Link] R42_R_0603_1608Metric_e00ced120b5b_ln_007  label="R25_R_0603_1608Metric_14260ea3fd4e"
  LinkPlacement = pos=(64.77,-44.704,-1.6) rot=(0,1,0;3.14159rad)
  LinkedObject = -> Shape002
  Placement = pos=(64.77,-44.704,-1.6) rot=(0,1,0;3.14159rad)
FEATURE [Part::Feature] Shape007  label="U10_MSOP_8_3x3mm_P065mm_82bb67e16242"
  Placement = pos=(63.5,-23.241,-1.6) rot=(0.707107,0.707107,0;3.14159rad)
  shape: bbox 3 x 4.9 x 0.95 mm, 156 faces (baked)
FEATURE [App::Link] U2_SOT_23_5143090a7d01_ln_001  label="Q1_SOT_23_1223d9ad7d7e"
  LinkPlacement = pos=(68.072,-33.274,-1.6) rot=(1,0,0;3.14159rad)
  LinkedObject = -> Shape005
  Placement = pos=(68.072,-33.274,-1.6) rot=(1,0,0;3.14159rad)
FEATURE [App::Link] C19_C_0805_2012Metric_915db11c73f1_ln_002  label="C11_C_0805_2012Metric_20aa78c893d6"
  LinkPlacement = pos=(54.2075,-49.53,-1.6) rot=(0,1,0;3.14159rad)
  LinkedObject = -> Shape
  Placement = pos=(54.2075,-49.53,-1.6) rot=(0,1,0;3.14159rad)
FEATURE [Part::Feature] Shape008  label="J3_PinHeader_2x05_P127mm_Vertical_4a0e541a8516"
  Placement = pos=(75.819,-54.473,-1.6) rot=(0,1,0;3.14159rad)
  shape: bbox 3.4 x 6.35 x 6.3 mm, 214 faces (baked)
FEATURE [App::Link] R42_R_0603_1608Metric_e00ced120b5b_ln_008  label="R1_R_0603_1608Metric_52185c8e4965"
  LinkPlacement = pos=(27.265,-22.733,-1.6) rot=(1,0,0;3.14159rad)
  LinkedObject = -> Shape002
  Placement = pos=(27.265,-22.733,-1.6) rot=(1,0,0;3.14159rad)
FEATURE [App::Link] C19_C_0805_2012Metric_915db11c73f1_ln_003  label="C7_C_0805_2012Metric_b3b50e9b0364"
  LinkPlacement = pos=(50.2705,-49.53,-1.6) rot=(1,0,0;3.14159rad)
  LinkedObject = -> Shape
  Placement = pos=(50.2705,-49.53,-1.6) rot=(1,0,0;3.14159rad)
FEATURE [App::Link] U10_MSOP_8_3x3mm_P065mm_82bb67e16242_ln_  label="U9_MSOP_8_3x3mm_P065mm_9b50181ec5fb"
  LinkPlacement = pos=(57.023,-41.91,-1.6) rot=(1,0,0;3.14159rad)
  LinkedObject = -> Shape007
  Placement = pos=(57.023,-41.91,-1.6) rot=(1,0,0;3.14159rad)
FEATURE [App::Link] _2VGood1_LED_0805_2012Metric_2ad75f4ca093_ln_  label="5VGood1_LED_0805_2012Metric_60cda601a8c1"
  LinkPlacement = pos=(51.943,-60.96,-1.6) rot=(0,1,0;3.14159rad)
  LinkedObject = -> Shape006
  Placement = pos=(51.943,-60.96,-1.6) rot=(0,1,0;3.14159rad)
FEATURE [App::Link] U2_SOT_23_5143090a7d01_ln_002  label="Q3_SOT_23_1241f12d323f"
  LinkPlacement = pos=(59.055,-32.766,-1.6) rot=(1,0,0;3.14159rad)
  LinkedObject = -> Shape005
  Placement = pos=(59.055,-32.766,-1.6) rot=(1,0,0;3.14159rad)
FEATURE [App::Link] C18_C_0603_1608Metric_10e447ca614a_ln_004  label="C2_C_0603_1608Metric_784de1c4b5be"
  LinkPlacement = pos=(27.178,-37.28,-1.6) rot=(0.707107,0.707107,0;3.14159rad)
  LinkedObject = -> Shape001
  Placement = pos=(27.178,-37.28,-1.6) rot=(0.707107,0.707107,0;3.14159rad)
FEATURE [Part::Feature] Shape009  label="D10_D_SOD_323_1cf1e5386782"
  Placement = pos=(31.369,-61.087,-1.6) rot=(1,0,0;3.14159rad)
  shape: bbox 2.5 x 1.25 x 1.1 mm, 67 faces (baked)
FEATURE [App::Link] D10_D_SOD_323_1cf1e5386782_ln_  label="D8_D_SOD_323_442fc4d99dd7"
  LinkPlacement = pos=(52.324,-24.257,-1.6) rot=(1,0,0;3.14159rad)
  LinkedObject = -> Shape009
  Placement = pos=(52.324,-24.257,-1.6) rot=(1,0,0;3.14159rad)
FEATURE [App::Link] R42_R_0603_1608Metric_e00ced120b5b_ln_009  label="R46_R_0603_1608Metric_d391e1cc1bf8"
  LinkPlacement = pos=(55.88,-18.923,-1.6) rot=(1,0,0;3.14159rad)
  LinkedObject = -> Shape002
  Placement = pos=(55.88,-18.923,-1.6) rot=(1,0,0;3.14159rad)
FEATURE [App::Link] R42_R_0603_1608Metric_e00ced120b5b_ln_010  label="R44_R_0603_1608Metric_76086e2af044"
  LinkPlacement = pos=(70.993,-21.59,-1.6) rot=(0,1,0;3.14159rad)
  LinkedObject = -> Shape002
  Placement = pos=(70.993,-21.59,-1.6) rot=(0,1,0;3.14159rad)
FEATURE [App::Link] R42_R_0603_1608Metric_e00ced120b5b_ln_011  label="R24_R_0603_1608Metric_616434719463"
  LinkPlacement = pos=(62.357,-43.815,-1.6) rot=(0.707107,-0.707107,0;3.14159rad)
  LinkedObject = -> Shape002
  Placement = pos=(62.357,-43.815,-1.6) rot=(0.707107,-0.707107,0;3.14159rad)
FEATURE [App::Link] U2_SOT_23_5143090a7d01_ln_003  label="Q6_SOT_23_f7e973546728"
  LinkPlacement = pos=(67.31,-23.876,-1.6) rot=(1,0,0;3.14159rad)
  LinkedObject = -> Shape005
  Placement = pos=(67.31,-23.876,-1.6) rot=(1,0,0;3.14159rad)
FEATURE [App::Link] C18_C_0603_1608Metric_10e447ca614a_ln_005  label="C31_C_0603_1608Metric_179902ffe984"
  LinkPlacement = pos=(58.801,-24.638,-1.6) rot=(1,0,0;3.14159rad)
  LinkedObject = -> Shape001
  Placement = pos=(58.801,-24.638,-1.6) rot=(1,0,0;3.14159rad)
FEATURE [App::Link] C18_C_0603_1608Metric_10e447ca614a_ln_006  label="C25_C_0603_1608Metric_a51b3fc9b87c"
  LinkPlacement = pos=(48.26,-46.101,-1.6) rot=(1,0,0;3.14159rad)
  LinkedObject = -> Shape001
  Placement = pos=(48.26,-46.101,-1.6) rot=(1,0,0;3.14159rad)
FEATURE [App::Link] J3_PinHeader_2x05_P127mm_Vertical_4a0e541a8516_ln_  label="J5_PinHeader_2x05_P127mm_Vertical_21cfdfc90ae7"
  LinkPlacement = pos=(16.891,-54.483,-1.6) rot=(0,1,0;3.14159rad)
  LinkedObject = -> Shape008
  Placement = pos=(16.891,-54.483,-1.6) rot=(0,1,0;3.14159rad)
FEATURE [App::Link] D10_D_SOD_323_1cf1e5386782_ln_001  label="D2_D_SOD_323_81fae5dc7b6e"
  LinkPlacement = pos=(47.371,-48.895,-1.6) rot=(0.707107,0.707107,0;3.14159rad)
  LinkedObject = -> Shape009
  Placement = pos=(47.371,-48.895,-1.6) rot=(0.707107,0.707107,0;3.14159rad)
FEATURE [App::Link] R42_R_0603_1608Metric_e00ced120b5b_ln_012  label="R28_R_0603_1608Metric_524fb33c0c76"
  LinkPlacement = pos=(59.7385,-49.596,-1.6) rot=(0.707107,0.707107,0;3.14159rad)
  LinkedObject = -> Shape002
  Placement = pos=(59.7385,-49.596,-1.6) rot=(0.707107,0.707107,0;3.14159rad)
FEATURE [App::Link] R42_R_0603_1608Metric_e00ced120b5b_ln_013  label="R9_R_0603_1608Metric_39820daff148"
  LinkPlacement = pos=(31.877,-18.607,-1.6) rot=(0.707107,0.707107,0;3.14159rad)
  LinkedObject = -> Shape002
  Placement = pos=(31.877,-18.607,-1.6) rot=(0.707107,0.707107,0;3.14159rad)
FEATURE [App::Link] C18_C_0603_1608Metric_10e447ca614a_ln_007  label="C28_C_0603_1608Metric_9930d46ac3f8"
  LinkPlacement = pos=(53.467,-18.288,-1.6) rot=(0.707107,0.707107,0;3.14159rad)
  LinkedObject = -> Shape001
  Placement = pos=(53.467,-18.288,-1.6) rot=(0.707107,0.707107,0;3.14159rad)
FEATURE [App::Link] R42_R_0603_1608Metric_e00ced120b5b_ln_014  label="R23_R_0603_1608Metric_14708d2771e9"
  LinkPlacement = pos=(68.199,-51.308,-1.6) rot=(0.707107,-0.707107,0;3.14159rad)
  LinkedObject = -> Shape002
  Placement = pos=(68.199,-51.308,-1.6) rot=(0.707107,-0.707107,0;3.14159rad)
FEATURE [App::Link] C19_C_0805_2012Metric_915db11c73f1_ln_004  label="C23_C_0805_2012Metric_29fb196ac7a2"
  LinkPlacement = pos=(70.231,-40.386,-1.6) rot=(0,1,0;3.14159rad)
  LinkedObject = -> Shape
  Placement = pos=(70.231,-40.386,-1.6) rot=(0,1,0;3.14159rad)
FEATURE [Part::Feature] Shape010  label="U1_Converter_DCDC_RECOM_R_78E_05_THT_7495ffbcc0e0"
  Placement = pos=(49.877,-53.213,-1.6) rot=(1,0,0;3.14159rad)
  shape: bbox 11.67 x 8.57 x 14.5 mm, 27 faces (baked)
FEATURE [App::Link] _2VGood1_LED_0805_2012Metric_2ad75f4ca093_ln_001  label="Error1_LED_0805_2012Metric_0193bb44fb5e"
  LinkPlacement = pos=(23.455,-19.939,-1.6) rot=(0,1,0;3.14159rad)
  LinkedObject = -> Shape006
  Placement = pos=(23.455,-19.939,-1.6) rot=(0,1,0;3.14159rad)
FEATURE [App::Link] C19_C_0805_2012Metric_915db11c73f1_ln_005  label="C15_C_0805_2012Metric_c2950c4f82bb"
  LinkPlacement = pos=(45.339,-49.022,-1.6) rot=(0.707107,0.707107,0;3.14159rad)
  LinkedObject = -> Shape
  Placement = pos=(45.339,-49.022,-1.6) rot=(0.707107,0.707107,0;3.14159rad)
FEATURE [App::Link] R42_R_0603_1608Metric_e00ced120b5b_ln_015  label="R11_R_0603_1608Metric_fc6ec5a46fb0"
  LinkPlacement = pos=(44.45,-16.699,-1.6) rot=(1,0,0;3.14159rad)
  LinkedObject = -> Shape002
  Placement = pos=(44.45,-16.699,-1.6) rot=(1,0,0;3.14159rad)
FEATURE [App::Link] R42_R_0603_1608Metric_e00ced120b5b_ln_016  label="R43_R_0603_1608Metric_bffcf2708168"
  LinkPlacement = pos=(65.786,-17.907,-1.6) rot=(0,1,0;3.14159rad)
  LinkedObject = -> Shape002
  Placement = pos=(65.786,-17.907,-1.6) rot=(0,1,0;3.14159rad)
FEATURE [App::Link] D10_D_SOD_323_1cf1e5386782_ln_002  label="D3_D_SOD_323_b8dc3af82ad9"
  LinkPlacement = pos=(58.674,-22.225,-1.6) rot=(1,0,0;3.14159rad)
  LinkedObject = -> Shape009
  Placement = pos=(58.674,-22.225,-1.6) rot=(1,0,0;3.14159rad)
FEATURE [App::Link] R42_R_0603_1608Metric_e00ced120b5b_ln_017  label="R38_R_0603_1608Metric_037dd372ccbc"
  LinkPlacement = pos=(70.739,-27.686,-1.6) rot=(0.707107,0.707107,0;3.14159rad)
  LinkedObject = -> Shape002
  Placement = pos=(70.739,-27.686,-1.6) rot=(0.707107,0.707107,0;3.14159rad)
FEATURE [App::Link] C19_C_0805_2012Metric_915db11c73f1_ln_006  label="C20_C_0805_2012Metric_feb99ca7776e"
  LinkPlacement = pos=(31.877,-15.686,-1.6) rot=(0,1,0;3.14159rad)
  LinkedObject = -> Shape
  Placement = pos=(31.877,-15.686,-1.6) rot=(0,1,0;3.14159rad)
FEATURE [App::Link] R42_R_0603_1608Metric_e00ced120b5b_ln_018  label="R37_R_0603_1608Metric_1e3016d2806e"
  LinkPlacement = pos=(70.993,-23.241,-1.6) rot=(0,1,0;3.14159rad)
  LinkedObject = -> Shape002
  Placement = pos=(70.993,-23.241,-1.6) rot=(0,1,0;3.14159rad)
FEATURE [Part::Feature] Shape011  label="U7_SOIC_8_39x49mm_P127mm_1499a48e6e93"
  Placement = pos=(44.45,-21.209,-1.6) rot=(0.707107,0.707107,0;3.14159rad)
  shape: bbox 4.9 x 6 x 1.75 mm, 156 faces (baked)
FEATURE [App::Link] R42_R_0603_1608Metric_e00ced120b5b_ln_019  label="R10_R_0603_1608Metric_863b16e2652c"
  LinkPlacement = pos=(48.133,-19.558,-1.6) rot=(0.707107,0.707107,0;3.14159rad)
  LinkedObject = -> Shape002
  Placement = pos=(48.133,-19.558,-1.6) rot=(0.707107,0.707107,0;3.14159rad)
FEATURE [App::Link] R42_R_0603_1608Metric_e00ced120b5b_ln_020  label="R7_R_0603_1608Metric_1723f24f5f2f"
  LinkPlacement = pos=(78.105,-43.688,-1.6) rot=(0.707107,0.707107,0;3.14159rad)
  LinkedObject = -> Shape002
  Placement = pos=(78.105,-43.688,-1.6) rot=(0.707107,0.707107,0;3.14159rad)
FEATURE [App::Link] C18_C_0603_1608Metric_10e447ca614a_ln_008  label="C4_C_0603_1608Metric_5f5500ef63df"
  LinkPlacement = pos=(32.131,-25.146,-1.6) rot=(0,1,0;3.14159rad)
  LinkedObject = -> Shape001
  Placement = pos=(32.131,-25.146,-1.6) rot=(0,1,0;3.14159rad)
FEATURE [App::Link] R42_R_0603_1608Metric_e00ced120b5b_ln_021  label="R17_R_0603_1608Metric_fc738fbfad18"
  LinkPlacement = pos=(70.739,-30.988,-1.6) rot=(0.707107,0.707107,0;3.14159rad)
  LinkedObject = -> Shape002
  Placement = pos=(70.739,-30.988,-1.6) rot=(0.707107,0.707107,0;3.14159rad)
FEATURE [App::Link] U2_SOT_23_5143090a7d01_ln_004  label="Q7_SOT_23_bc60db84acee"
  LinkPlacement = pos=(63.627,-29.845,-1.6) rot=(1,0,0;3.14159rad)
  LinkedObject = -> Shape005
  Placement = pos=(63.627,-29.845,-1.6) rot=(1,0,0;3.14159rad)
FEATURE [App::Link] U1_Converter_DCDC_RECOM_R_78E_05_THT_7495ffbcc0e0_ln_  label="U5_Converter_DCDC_RECOM_R_78E_05_THT_6eb4cbfbcd04"
  LinkPlacement = pos=(36.542,-53.213,-1.6) rot=(1,0,0;3.14159rad)
  LinkedObject = -> Shape010
  Placement = pos=(36.542,-53.213,-1.6) rot=(1,0,0;3.14159rad)
FEATURE [App::Link] R42_R_0603_1608Metric_e00ced120b5b_ln_022  label="R26_R_0603_1608Metric_34ca61038909"
  LinkPlacement = pos=(67.691,-28.829,-1.6) rot=(0.707107,-0.707107,0;3.14159rad)
  LinkedObject = -> Shape002
  Placement = pos=(67.691,-28.829,-1.6) rot=(0.707107,-0.707107,0;3.14159rad)
FEATURE [App::Link] R42_R_0603_1608Metric_e00ced120b5b_ln_023  label="R27_R_0603_1608Metric_60e756865c77"
  LinkPlacement = pos=(67.183,-43.815,-1.6) rot=(0.707107,0.707107,0;3.14159rad)
  LinkedObject = -> Shape002
  Placement = pos=(67.183,-43.815,-1.6) rot=(0.707107,0.707107,0;3.14159rad)
FEATURE [App::Link] R42_R_0603_1608Metric_e00ced120b5b_ln_024  label="R14_R_0603_1608Metric_d767aa6e1c7e"
  LinkPlacement = pos=(58.928,-37.592,-1.6) rot=(0,1,0;3.14159rad)
  LinkedObject = -> Shape002
  Placement = pos=(58.928,-37.592,-1.6) rot=(0,1,0;3.14159rad)
FEATURE [App::Link] R42_R_0603_1608Metric_e00ced120b5b_ln_025  label="R35_R_0603_1608Metric_a89be60451e6"
  LinkPlacement = pos=(67.056,-26.416,-1.6) rot=(0,1,0;3.14159rad)
  LinkedObject = -> Shape002
  Placement = pos=(67.056,-26.416,-1.6) rot=(0,1,0;3.14159rad)
FEATURE [App::Link] R42_R_0603_1608Metric_e00ced120b5b_ln_026  label="R12_R_0603_1608Metric_98ba704dd8f1"
  LinkPlacement = pos=(65.786,-41.402,-1.6) rot=(0,1,0;3.14159rad)
  LinkedObject = -> Shape002
  Placement = pos=(65.786,-41.402,-1.6) rot=(0,1,0;3.14159rad)
FEATURE [App::Link] C18_C_0603_1608Metric_10e447ca614a_ln_009  label="C1_C_0603_1608Metric_84c5a7f979f1"
  LinkPlacement = pos=(32.131,-23.495,-1.6) rot=(0,1,0;3.14159rad)
  LinkedObject = -> Shape001
  Placement = pos=(32.131,-23.495,-1.6) rot=(0,1,0;3.14159rad)
FEATURE [App::Link] U2_SOT_23_5143090a7d01_ln_005  label="Q5_SOT_23_2fb3d1e9febb"
  LinkPlacement = pos=(62.9135,-49.596,-1.6) rot=(1,0,0;3.14159rad)
  LinkedObject = -> Shape005
  Placement = pos=(62.9135,-49.596,-1.6) rot=(1,0,0;3.14159rad)
FEATURE [App::Link] _2VGood1_LED_0805_2012Metric_2ad75f4ca093_ln_002  label="Heart1_LED_0805_2012Metric_c9bdaa238e08"
  LinkPlacement = pos=(23.455,-22.733,-1.6) rot=(0,1,0;3.14159rad)
  LinkedObject = -> Shape006
  Placement = pos=(23.455,-22.733,-1.6) rot=(0,1,0;3.14159rad)
FEATURE [App::Link] C18_C_0603_1608Metric_10e447ca614a_ln_010  label="C8_C_0603_1608Metric_bdc2e3e24877"
  LinkPlacement = pos=(39.116,-25.973,-1.6) rot=(0,1,0;3.14159rad)
  LinkedObject = -> Shape001
  Placement = pos=(39.116,-25.973,-1.6) rot=(0,1,0;3.14159rad)
FEATURE [App::Link] C19_C_0805_2012Metric_915db11c73f1_ln_007  label="C22_C_0805_2012Metric_28f6afd9b51f"
  LinkPlacement = pos=(69.977,-54.61,-1.6) rot=(0,1,0;3.14159rad)
  LinkedObject = -> Shape
  Placement = pos=(69.977,-54.61,-1.6) rot=(0,1,0;3.14159rad)
FEATURE [App::Link] C18_C_0603_1608Metric_10e447ca614a_ln_011  label="C3_C_0603_1608Metric_22f7aa9a1690"
  LinkPlacement = pos=(27.178,-33.782,-1.6) rot=(0.707107,-0.707107,0;3.14159rad)
  LinkedObject = -> Shape001
  Placement = pos=(27.178,-33.782,-1.6) rot=(0.707107,-0.707107,0;3.14159rad)
FEATURE [App::Link] R42_R_0603_1608Metric_e00ced120b5b_ln_027  label="R20_R_0603_1608Metric_2b4dd9f72b59"
  LinkPlacement = pos=(57.404,-39.116,-1.6) rot=(1,0,0;3.14159rad)
  LinkedObject = -> Shape002
  Placement = pos=(57.404,-39.116,-1.6) rot=(1,0,0;3.14159rad)
FEATURE [App::Link] R42_R_0603_1608Metric_e00ced120b5b_ln_028  label="R8_R_0603_1608Metric_7230250cfa97"
  LinkPlacement = pos=(69.596,-38.354,-1.6) rot=(1,0,0;3.14159rad)
  LinkedObject = -> Shape002
  Placement = pos=(69.596,-38.354,-1.6) rot=(1,0,0;3.14159rad)
FEATURE [App::Link] R42_R_0603_1608Metric_e00ced120b5b_ln_029  label="R6_R_0603_1608Metric_956f91f139f8"
  LinkPlacement = pos=(43.434,-60.96,-1.6) rot=(1,0,0;3.14159rad)
  LinkedObject = -> Shape002
  Placement = pos=(43.434,-60.96,-1.6) rot=(1,0,0;3.14159rad)
FEATURE [App::Link] R42_R_0603_1608Metric_e00ced120b5b_ln_030  label="R15_R_0603_1608Metric_29f9765fedca"
  LinkPlacement = pos=(57.15,-36.068,-1.6) rot=(0,1,0;3.14159rad)
  LinkedObject = -> Shape002
  Placement = pos=(57.15,-36.068,-1.6) rot=(0,1,0;3.14159rad)
FEATURE [App::Link] _2VGood1_LED_0805_2012Metric_2ad75f4ca093_ln_003  label="3V3Good1_LED_0805_2012Metric_f770177cd55f"
  LinkPlacement = pos=(39.624,-60.96,-1.6) rot=(1,0,0;3.14159rad)
  LinkedObject = -> Shape006
  Placement = pos=(39.624,-60.96,-1.6) rot=(1,0,0;3.14159rad)
FEATURE [App::Link] R42_R_0603_1608Metric_e00ced120b5b_ln_031  label="R13_R_0603_1608Metric_88249867bc70"
  LinkPlacement = pos=(64.389,-33.528,-1.6) rot=(0,1,0;3.14159rad)
  LinkedObject = -> Shape002
  Placement = pos=(64.389,-33.528,-1.6) rot=(0,1,0;3.14159rad)
FEATURE [App::Link] R42_R_0603_1608Metric_e00ced120b5b_ln_032  label="R18_R_0603_1608Metric_e7deeba773bd"
  LinkPlacement = pos=(54.991,-33.655,-1.6) rot=(0,1,0;3.14159rad)
  LinkedObject = -> Shape002
  Placement = pos=(54.991,-33.655,-1.6) rot=(0,1,0;3.14159rad)
FEATURE [App::Link] R42_R_0603_1608Metric_e00ced120b5b_ln_033  label="R41_R_0603_1608Metric_2dfa8f3c3e90"
  LinkPlacement = pos=(59.436,-18.796,-1.6) rot=(0.707107,-0.707107,0;3.14159rad)
  LinkedObject = -> Shape002
  Placement = pos=(59.436,-18.796,-1.6) rot=(0.707107,-0.707107,0;3.14159rad)
FEATURE [App::Link] C18_C_0603_1608Metric_10e447ca614a_ln_012  label="C30_C_0603_1608Metric_0742e3473aaa"
  LinkPlacement = pos=(50.8,-41.402,-1.6) rot=(0,1,0;3.14159rad)
  LinkedObject = -> Shape001
  Placement = pos=(50.8,-41.402,-1.6) rot=(0,1,0;3.14159rad)
FEATURE [App::Link] R42_R_0603_1608Metric_e00ced120b5b_ln_034  label="R21_R_0603_1608Metric_9688ea295803"
  LinkPlacement = pos=(51.308,-36.957,-1.6) rot=(1,0,0;3.14159rad)
  LinkedObject = -> Shape002
  Placement = pos=(51.308,-36.957,-1.6) rot=(1,0,0;3.14159rad)
FEATURE [App::Link] J3_PinHeader_2x05_P127mm_Vertical_4a0e541a8516_ln_001  label="J4_PinHeader_2x05_P127mm_Vertical_89510c161731"
  LinkPlacement = pos=(16.129,-20.701,-1.6) rot=(1,0,0;3.14159rad)
  LinkedObject = -> Shape008
  Placement = pos=(16.129,-20.701,-1.6) rot=(1,0,0;3.14159rad)
FEATURE [Part::Feature] Part__Feature  label="932d09b3-9c39-11ed-93f0-dde97e994e83_part"
  shape: bbox 6.22 x 6.5 x 2.3 mm, 13 faces (baked)
FEATURE [App::Part] _32d09b3_9c39_11ed_93f0_dde97e994e83  label="932d09b3-9c39-11ed-93f0-dde97e994e83"
  Group = -> [Part__Feature]
  Origin = -> Origin008
FEATURE [Part::Feature] Part__Feature001  label="932d09b4-9c39-11ed-93f0-dde97e994e83_part"
  shape: bbox 5.24 x 5.4 x 0.5 mm, 16 faces (baked)
FEATURE [App::Part] _32d09b4_9c39_11ed_93f0_dde97e994e83  label="932d09b4-9c39-11ed-93f0-dde97e994e83"
  Group = -> [Part__Feature001]
  Origin = -> Origin009
FEATURE [Part::Feature] Part__Feature002  label="932d09b5-9c39-11ed-93f0-dde97e994e83_part"
  shape: bbox 3.552 x 0.99 x 1.44 mm, 22 faces (baked)
FEATURE [Part::Feature] Part__Feature003  label="932d09b5-9c39-11ed-93f0-dde97e994e83_part001"
  shape: bbox 1.672 x 0.99 x 0.5 mm, 10 faces (baked)
FEATURE [Part::Feature] Part__Feature004  label="932d09b5-9c39-11ed-93f0-dde97e994e83_part002"
  shape: bbox 3.552 x 0.99 x 1.44 mm, 22 faces (baked)
FEATURE [App::Part] _32d09b5_9c39_11ed_93f0_dde97e994e83_part  label="932d09b5-9c39-11ed-93f0-dde97e994e83_part003"
  Group = -> [Part__Feature002,Part__Feature003,Part__Feature004]
  Origin = -> Origin010
FEATURE [App::Part] _32d09b5_9c39_11ed_93f0_dde97e994e83  label="932d09b5-9c39-11ed-93f0-dde97e994e83"
  Group = -> [_32d09b5_9c39_11ed_93f0_dde97e994e83_part]
  Origin = -> Origin011
FEATURE [App::Part] _32d09b2_9c39_11ed_93f0_dde97e994e83  label="932d09b2-9c39-11ed-93f0-dde97e994e83"
  Group = -> [_32d09b3_9c39_11ed_93f0_dde97e994e83,_32d09b4_9c39_11ed_93f0_dde97e994e83,_32d09b5_9c39_11ed_93f0_dde97e994e83]
  Origin = -> Origin012
FEATURE [App::Part] CQ_assembly  label="U8_CQ assembly_9e30a5f4f37c"
  Group = -> [_32d09b2_9c39_11ed_93f0_dde97e994e83]
  Origin = -> Origin013
  Placement = pos=(73.025,-46.472,-1.6) rot=(0.707107,0.707107,0;3.14159rad)
FEATURE [App::Link] C19_C_0805_2012Metric_915db11c73f1_ln_008  label="C26_C_0805_2012Metric_58a7a7612ec2"
  LinkPlacement = pos=(57.15,-47.244,-1.6) rot=(0.707107,-0.707107,0;3.14159rad)
  LinkedObject = -> Shape
  Placement = pos=(57.15,-47.244,-1.6) rot=(0.707107,-0.707107,0;3.14159rad)
FEATURE [App::Link] R42_R_0603_1608Metric_e00ced120b5b_ln_035  label="R19_R_0603_1608Metric_4285ec9b66e1"
  LinkPlacement = pos=(54.483,-36.957,-1.6) rot=(0.707107,-0.707107,0;3.14159rad)
  LinkedObject = -> Shape002
  Placement = pos=(54.483,-36.957,-1.6) rot=(0.707107,-0.707107,0;3.14159rad)
FEATURE [App::Link] U2_SOT_23_5143090a7d01_ln_006  label="Q8_SOT_23_4a5958cf5442"
  LinkPlacement = pos=(69.85,-17.526,-1.6) rot=(1,0,0;3.14159rad)
  LinkedObject = -> Shape005
  Placement = pos=(69.85,-17.526,-1.6) rot=(1,0,0;3.14159rad)
FEATURE [App::Link] R42_R_0603_1608Metric_e00ced120b5b_ln_036  label="R33_R_0603_1608Metric_c9c509e34e71"
  LinkPlacement = pos=(49.149,-44.577,-1.6) rot=(0,1,0;3.14159rad)
  LinkedObject = -> Shape002
  Placement = pos=(49.149,-44.577,-1.6) rot=(0,1,0;3.14159rad)
FEATURE [App::Link] R42_R_0603_1608Metric_e00ced120b5b_ln_037  label="R34_R_0603_1608Metric_85fe14c106d9"
  LinkPlacement = pos=(53.848,-27.686,-1.6) rot=(1,0,0;3.14159rad)
  LinkedObject = -> Shape002
  Placement = pos=(53.848,-27.686,-1.6) rot=(1,0,0;3.14159rad)
FEATURE [App::Link] R42_R_0603_1608Metric_e00ced120b5b_ln_038  label="R16_R_0603_1608Metric_68531f109549"
  LinkPlacement = pos=(62.357,-37.592,-1.6) rot=(0,1,0;3.14159rad)
  LinkedObject = -> Shape002
  Placement = pos=(62.357,-37.592,-1.6) rot=(0,1,0;3.14159rad)
FEATURE [App::Link] U2_SOT_23_5143090a7d01_ln_007  label="Q4_SOT_23_94e1ef1df5d7"
  LinkPlacement = pos=(67.183,-47.625,-1.6) rot=(0.707107,0.707107,0;3.14159rad)
  LinkedObject = -> Shape005
  Placement = pos=(67.183,-47.625,-1.6) rot=(0.707107,0.707107,0;3.14159rad)
FEATURE [App::Link] D10_D_SOD_323_1cf1e5386782_ln_003  label="D5_D_SOD_323_d6054b8cd4c7"
  LinkPlacement = pos=(49.911,-19.558,-1.6) rot=(0.707107,-0.707107,0;3.14159rad)
  LinkedObject = -> Shape009
  Placement = pos=(49.911,-19.558,-1.6) rot=(0.707107,-0.707107,0;3.14159rad)
FEATURE [App::Link] D10_D_SOD_323_1cf1e5386782_ln_004  label="D4_D_SOD_323_bdc2fbd66cdd"
  LinkPlacement = pos=(53.848,-15.24,-1.6) rot=(1,0,0;3.14159rad)
  LinkedObject = -> Shape009
  Placement = pos=(53.848,-15.24,-1.6) rot=(1,0,0;3.14159rad)
FEATURE [App::Link] C18_C_0603_1608Metric_10e447ca614a_ln_013  label="C10_C_0603_1608Metric_49a17912874c"
  LinkPlacement = pos=(41.529,-41.148,-1.6) rot=(0.707107,-0.707107,0;3.14159rad)
  LinkedObject = -> Shape001
  Placement = pos=(41.529,-41.148,-1.6) rot=(0.707107,-0.707107,0;3.14159rad)
FEATURE [App::Link] C18_C_0603_1608Metric_10e447ca614a_ln_014  label="C9_C_0603_1608Metric_ad1383201845"
  LinkPlacement = pos=(43.053,-40.132,-1.6) rot=(0.707107,-0.707107,0;3.14159rad)
  LinkedObject = -> Shape001
  Placement = pos=(43.053,-40.132,-1.6) rot=(0.707107,-0.707107,0;3.14159rad)
FEATURE [App::Link] R42_R_0603_1608Metric_e00ced120b5b_ln_039  label="R40_R_0603_1608Metric_03e1db1fd9d4"
  LinkPlacement = pos=(62.865,-27.178,-1.6) rot=(0,1,0;3.14159rad)
  LinkedObject = -> Shape002
  Placement = pos=(62.865,-27.178,-1.6) rot=(0,1,0;3.14159rad)
FEATURE [App::Link] D10_D_SOD_323_1cf1e5386782_ln_005  label="D1_D_SOD_323_7cfbc3cf6d88"
  LinkPlacement = pos=(52.197,-32.512,-1.6) rot=(0.707107,-0.707107,0;3.14159rad)
  LinkedObject = -> Shape009
  Placement = pos=(52.197,-32.512,-1.6) rot=(0.707107,-0.707107,0;3.14159rad)
FEATURE [App::Link] R42_R_0603_1608Metric_e00ced120b5b_ln_040  label="R32_R_0603_1608Metric_638f9ad5d960"
  LinkPlacement = pos=(51.816,-45.72,-1.6) rot=(0.707107,0.707107,0;3.14159rad)
  LinkedObject = -> Shape002
  Placement = pos=(51.816,-45.72,-1.6) rot=(0.707107,0.707107,0;3.14159rad)
FEATURE [App::Link] R42_R_0603_1608Metric_e00ced120b5b_ln_041  label="R5_R_0603_1608Metric_eab0520c1254"
  LinkPlacement = pos=(77.343,-46.99,-1.6) rot=(0.707107,-0.707107,0;3.14159rad)
  LinkedObject = -> Shape002
  Placement = pos=(77.343,-46.99,-1.6) rot=(0.707107,-0.707107,0;3.14159rad)
FEATURE [App::Link] R42_R_0603_1608Metric_e00ced120b5b_ln_042  label="R4_R_0603_1608Metric_1c33adfa3623"
  LinkPlacement = pos=(48.133,-60.96,-1.6) rot=(0,1,0;3.14159rad)
  LinkedObject = -> Shape002
  Placement = pos=(48.133,-60.96,-1.6) rot=(0,1,0;3.14159rad)
FEATURE [App::Link] C18_C_0603_1608Metric_10e447ca614a_ln_015  label="C16_C_0603_1608Metric_fd54e4cc6448"
  LinkPlacement = pos=(60.833,-14.986,-1.6) rot=(0,1,0;3.14159rad)
  LinkedObject = -> Shape001
  Placement = pos=(60.833,-14.986,-1.6) rot=(0,1,0;3.14159rad)
FEATURE [App::Link] J3_PinHeader_2x05_P127mm_Vertical_4a0e541a8516_ln_002  label="J2_PinHeader_2x05_P127mm_Vertical_e771ec2928c9"
  LinkPlacement = pos=(76.2,-14.859,-1.6) rot=(0,1,0;3.14159rad)
  LinkedObject = -> Shape008
  Placement = pos=(76.2,-14.859,-1.6) rot=(0,1,0;3.14159rad)
FEATURE [App::Link] C19_C_0805_2012Metric_915db11c73f1_ln_009  label="C27_C_0805_2012Metric_632f8fc273e4"
  LinkPlacement = pos=(55.372,-23.368,-1.6) rot=(0.707107,-0.707107,0;3.14159rad)
  LinkedObject = -> Shape
  Placement = pos=(55.372,-23.368,-1.6) rot=(0.707107,-0.707107,0;3.14159rad)
FEATURE [Part::Feature] Shape012  label="U3_LQFP_64_10x10mm_P05mm_ad08613fb525"
  Placement = pos=(36.576,-34.101,-1.6) rot=(1,0,0;3.14159rad)
  shape: bbox 12 x 12 x 1.5 mm, 1004 faces (baked)
FEATURE [App::Link] R42_R_0603_1608Metric_e00ced120b5b_ln_043  label="R45_R_0603_1608Metric_73e532b6d87c"
  LinkPlacement = pos=(69.469,-20.066,-1.6) rot=(0,1,0;3.14159rad)
  LinkedObject = -> Shape002
  Placement = pos=(69.469,-20.066,-1.6) rot=(0,1,0;3.14159rad)
FEATURE [App::Link] C18_C_0603_1608Metric_10e447ca614a_ln_016  label="C24_C_0603_1608Metric_f180910c596f"
  LinkPlacement = pos=(50.292,-32.893,-1.6) rot=(0.707107,-0.707107,0;3.14159rad)
  LinkedObject = -> Shape001
  Placement = pos=(50.292,-32.893,-1.6) rot=(0.707107,-0.707107,0;3.14159rad)
FEATURE [App::Link] R42_R_0603_1608Metric_e00ced120b5b_ln_044  label="R22_R_0603_1608Metric_74d0720be528"
  LinkPlacement = pos=(51.181,-35.433,-1.6) rot=(0,1,0;3.14159rad)
  LinkedObject = -> Shape002
  Placement = pos=(51.181,-35.433,-1.6) rot=(0,1,0;3.14159rad)
FEATURE [App::Link] R42_R_0603_1608Metric_e00ced120b5b_ln_045  label="R47_R_0603_1608Metric_036ee63e5562"
  LinkPlacement = pos=(55.88,-17.399,-1.6) rot=(0,1,0;3.14159rad)
  LinkedObject = -> Shape002
  Placement = pos=(55.88,-17.399,-1.6) rot=(0,1,0;3.14159rad)
FEATURE [App::Link] C21_CP_Radial_D80mm_P350mm_b4bb79b80bd8_ln_  label="C13_CP_Radial_D80mm_P350mm_7da63d23e92e"
  LinkPlacement = pos=(65.222,-55.753,-1.6) rot=(0,1,0;3.14159rad)
  LinkedObject = -> Shape003
  Placement = pos=(65.222,-55.753,-1.6) rot=(0,1,0;3.14159rad)
FEATURE [App::Part] Bot_e9e
  Group = -> [Shape,Shape001,Shape002,R42_R_0603_1608Metric_e00ced120b5b_ln_,R42_R_0603_1608Metric_e00ced120b5b_ln_001,Shape003,C19_C_0805_2012Metric_915db11c73f1_ln_,Shape004,R42_R_0603_1608Metric_e00ced120b5b_ln_002,C18_C_0603_1608Metric_10e447ca614a_ln_,R42_R_0603_1608Metric_e00ced120b5b_ln_003,R42_R_0603_1608Metric_e00ced120b5b_ln_004,Shape005,U2_SOT_23_5143090a7d01_ln_,+97 more]
  Origin = -> Origin004
FEATURE [App::Part] Step_Models_e9e
  Group = -> [Bot_e9e]
  Origin = -> Origin002
FEATURE [Part::Feature] pads_area001  label="topPads_e9e"
  Placement = pos=(0,0,0.02) rot=(0,0,1;0rad)
  shape: bbox 64.55 x 49.94 x 2e-07 mm, 250 faces, 0 solids (baked)
FEATURE [Part::Feature] Shape014  label="topTracks_e9e"
  Placement = pos=(0,0,0.01) rot=(0,0,1;0rad)
  shape: bbox 61.73 x 46.61 x 6.02e-05 mm, 42 faces, 0 solids (baked)
FEATURE [Part::Feature] zones_area001  label="topZones_e9e"
  Placement = pos=(0,0,0.01) rot=(0,0,1;0rad)
  shape: bbox 66.12 x 49.03 x 2e-07 mm, 6 faces, 0 solids (baked)
FEATURE [Part::Feature] pads_area003  label="botPads_e9e"
  Placement = pos=(0,0,-1.62) rot=(0,0,1;0rad)
  shape: bbox 64.55 x 49.94 x 2e-07 mm, 555 faces, 0 solids (baked)
FEATURE [Part::Feature] Shape016  label="botTracks_e9e"
  Placement = pos=(0,0,-1.61) rot=(0,0,1;0rad)
  shape: bbox 64.42 x 52.19 x 6.02e-05 mm, 194 faces, 0 solids (baked)
FEATURE [App::Part] Board_Geoms_e9e
  Group = -> [Pcb_e9e,PCB_Sketch_e9e,pads_area001,Shape014,zones_area001,pads_area003,Shape016]
  Origin = -> Origin
FEATURE [App::Part] Board_e9e  label="DIC"
  Group = -> [Local_CS_e9e,Board_Geoms_e9e,Step_Models_e9e]
  Origin = -> Origin001
